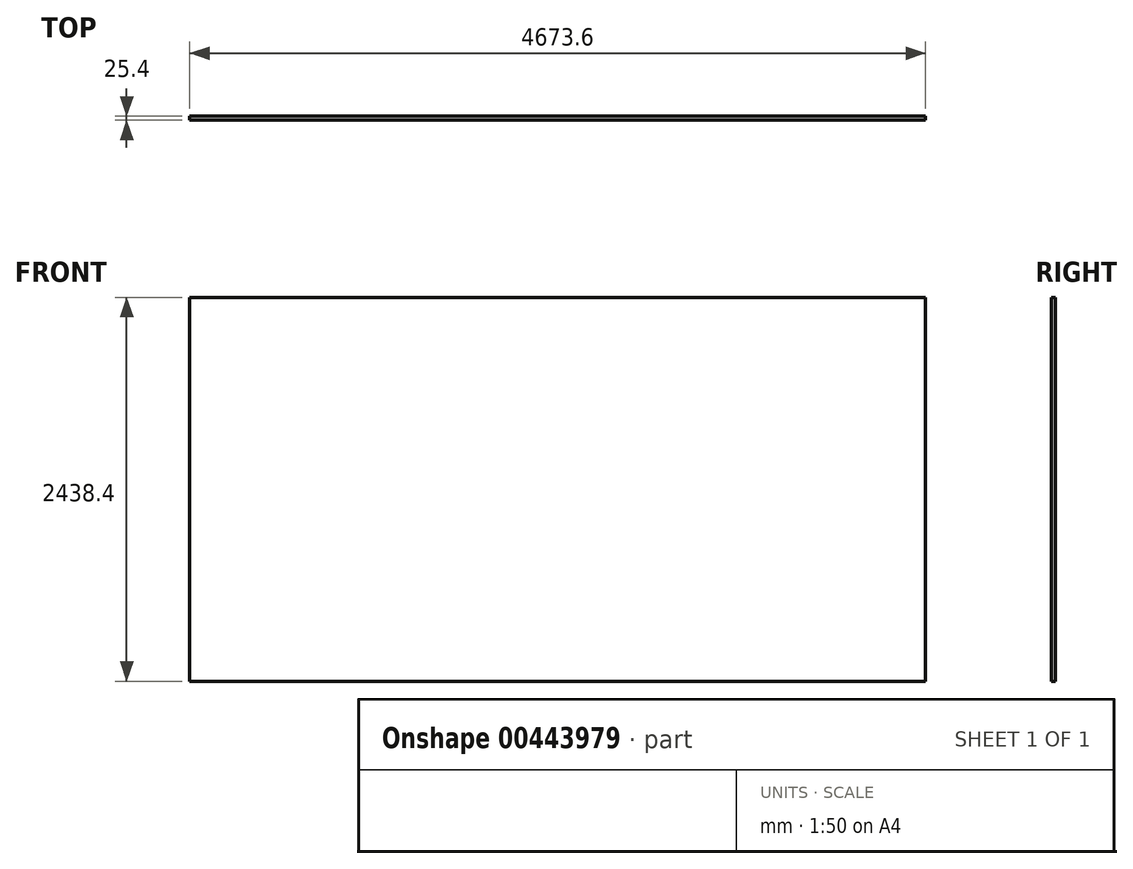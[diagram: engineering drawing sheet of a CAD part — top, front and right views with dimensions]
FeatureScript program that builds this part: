
annotation { "Feature Type Name" : "Feature", "Feature Type Description" : "" }
export const myFeature = defineFeature(function(context is Context, id is Id, definition is map)
    precondition{}
    {
        {
            var Q0;
            Q0=qCreatedBy(makeId("Front.planeOp"),FACE);
            var sketch = newSketch(context, id + "F0", { "sketchPlane" : qUnion([Q0])});
            skLineSegment(sketch, "E0.bottom", {"start": v(2336.8, -1219.2) * mm, "end": v(-2336.8, -1219.2) * mm});
            skLineSegment(sketch, "E0.top", {"start": v(2336.8, 1219.2) * mm, "end": v(-2336.8, 1219.2) * mm});
            skLineSegment(sketch, "E0.left", {"start": v(2336.8, -1219.2) * mm, "end": v(2336.8, 1219.2) * mm});
            skLineSegment(sketch, "E0.right", {"start": v(-2336.8, -1219.2) * mm, "end": v(-2336.8, 1219.2) * mm});
            skPoint(sketch, "E0.middle", {"position": v(0, 0) * mm});
            skSolve(sketch);
        }
        {
            var Q0;
            Q0=qSketchRegion(id+"F0",true);
            extrude(context, id + "F1", {"entities" : qUnion([Q0]), "depth" : 25.4 * mm});
        }
    });
